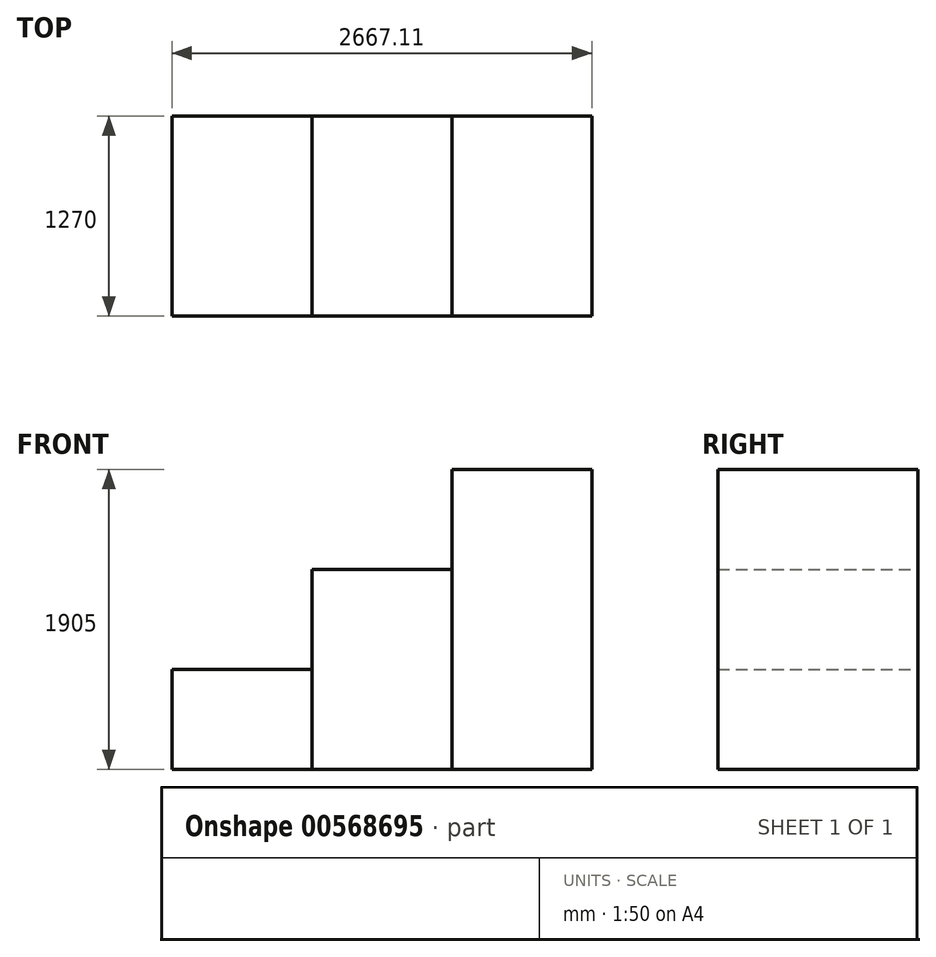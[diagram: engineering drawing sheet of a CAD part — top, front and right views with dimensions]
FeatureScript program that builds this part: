
annotation { "Feature Type Name" : "Feature", "Feature Type Description" : "" }
export const myFeature = defineFeature(function(context is Context, id is Id, definition is map)
    precondition{}
    {
        {
            var Q0;
            Q0=qCreatedBy(makeId("Front.planeOp"),FACE);
            var sketch = newSketch(context, id + "F0", { "sketchPlane" : qUnion([Q0])});
            skLineSegment(sketch, "E0.bottom", {"start": v(-558.24, 491.78) * mm, "end": v(330.76, 491.78) * mm});
            skLineSegment(sketch, "E0.top", {"start": v(-558.24, -143.22) * mm, "end": v(330.76, -143.22) * mm});
            skLineSegment(sketch, "E0.left", {"start": v(-558.24, 491.78) * mm, "end": v(-558.24, -143.22) * mm});
            skLineSegment(sketch, "E0.right", {"start": v(330.76, 491.78) * mm, "end": v(330.76, -143.22) * mm});
            skSolve(sketch);
        }
        {
            var Q0;
            Q0=qCreatedBy(makeId("Front.planeOp"),FACE);
            var sketch = newSketch(context, id + "F1", { "sketchPlane" : qUnion([Q0])});
            skLineSegment(sketch, "E1.bottom", {"start": v(330.82, -143.29) * mm, "end": v(1219.82, -143.29) * mm});
            skLineSegment(sketch, "E1.top", {"start": v(330.82, 1126.71) * mm, "end": v(1219.82, 1126.71) * mm});
            skLineSegment(sketch, "E1.left", {"start": v(330.82, -143.29) * mm, "end": v(330.82, 1126.71) * mm});
            skLineSegment(sketch, "E1.right", {"start": v(1219.82, -143.29) * mm, "end": v(1219.82, 1126.71) * mm});
            skSolve(sketch);
        }
        {
            var Q0;
            Q0=qCreatedBy(makeId("Front.planeOp"),FACE);
            var sketch = newSketch(context, id + "F2", { "sketchPlane" : qUnion([Q0])});
            skLineSegment(sketch, "E2.bottom", {"start": v(1219.87, -143.33) * mm, "end": v(2108.87, -143.33) * mm});
            skLineSegment(sketch, "E2.top", {"start": v(1219.87, 1761.67) * mm, "end": v(2108.87, 1761.67) * mm});
            skLineSegment(sketch, "E2.left", {"start": v(1219.87, -143.33) * mm, "end": v(1219.87, 1761.67) * mm});
            skLineSegment(sketch, "E2.right", {"start": v(2108.87, -143.33) * mm, "end": v(2108.87, 1761.67) * mm});
            skSolve(sketch);
        }
        {
            var Q0;
            Q0=makeQuery(id+"F0.imprint","IMPRINT",FACE,{"disambiguationData":[TD([[makeQuery(id+"F0.imprint","IMPRINT",EDGE,{"derivedFrom":sQuery(id+"F0.wireOp",EDGE,"E0.bottom")}),-1.0]])]});
            extrude(context, id + "F3", {"entities" : qUnion([Q0]), "depth" : 1270 * mm, "offsetDistance" : 25.4 * mm});
        }
        {
            var Q0;
            Q0=makeQuery(id+"F1.imprint","IMPRINT",FACE,{"disambiguationData":[TD([[makeQuery(id+"F1.imprint","IMPRINT",EDGE,{"derivedFrom":sQuery(id+"F1.wireOp",EDGE,"E1.bottom")}),1.0]])]});
            extrude(context, id + "F4", {"entities" : qUnion([Q0]), "depth" : 1270 * mm, "offsetDistance" : 25.4 * mm});
        }
        {
            var Q0;
            Q0=makeQuery(id+"F2.imprint","IMPRINT",FACE,{"disambiguationData":[TD([[makeQuery(id+"F2.imprint","IMPRINT",EDGE,{"derivedFrom":sQuery(id+"F2.wireOp",EDGE,"E2.bottom")}),1.0]])]});
            extrude(context, id + "F5", {"entities" : qUnion([Q0]), "depth" : 1270 * mm, "offsetDistance" : 25.4 * mm});
        }
    });
